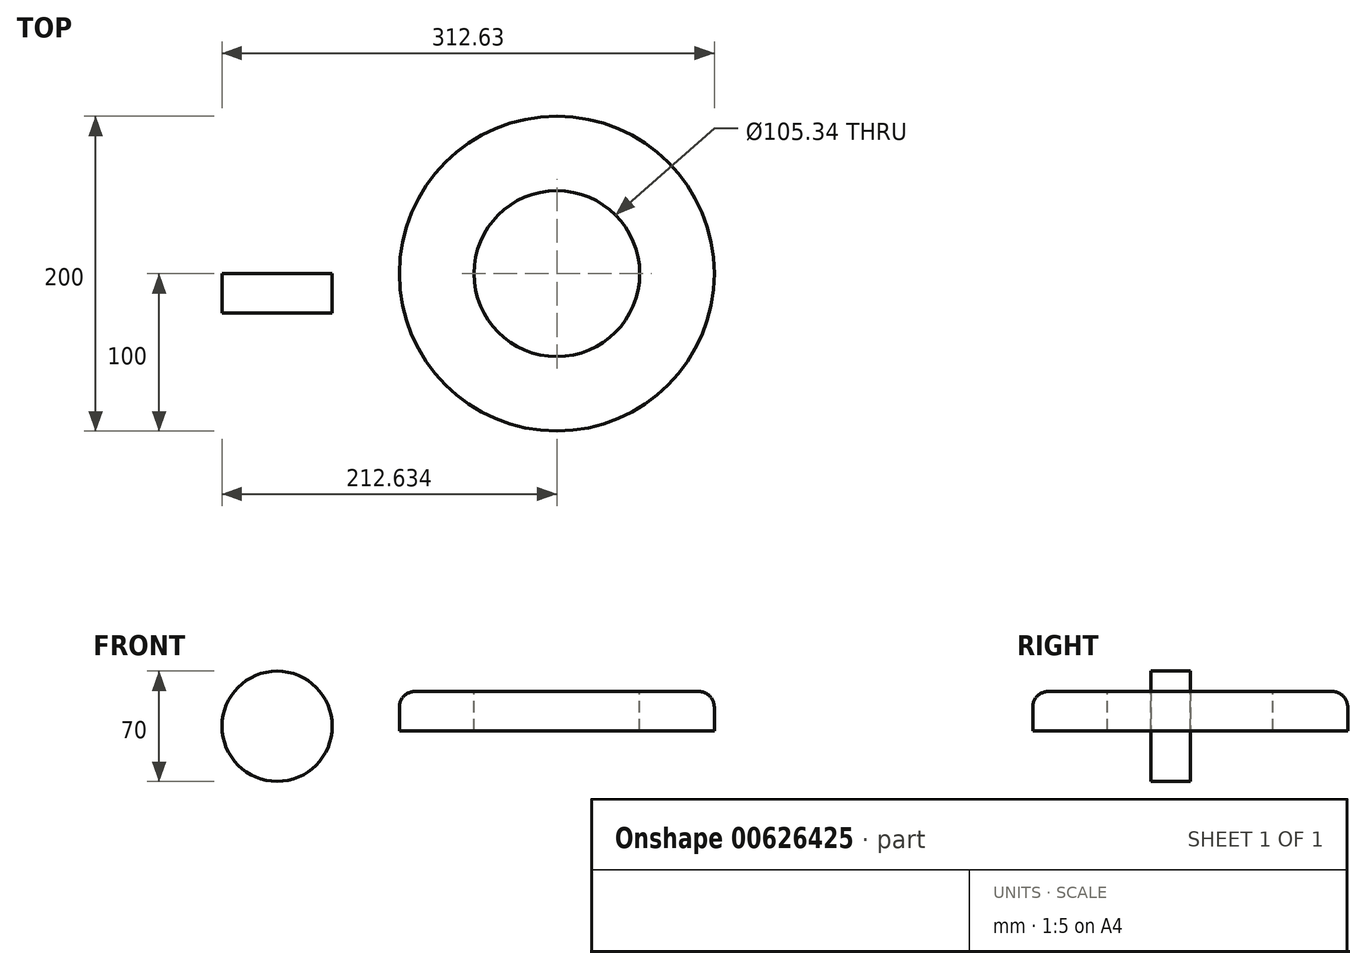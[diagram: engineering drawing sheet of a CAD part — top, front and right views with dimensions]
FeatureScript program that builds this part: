
annotation { "Feature Type Name" : "Feature", "Feature Type Description" : "" }
export const myFeature = defineFeature(function(context is Context, id is Id, definition is map)
    precondition{}
    {
        {
            var Q0;
            Q0=qCreatedBy(makeId("Front.planeOp"),FACE);
            var sketch = newSketch(context, id + "F0", { "sketchPlane" : qUnion([Q0])});
            skLineSegment(sketch, "E0.bottom", {"start": v(-39.69, 8.2) * mm, "end": v(60.31, 8.2) * mm});
            skLineSegment(sketch, "E0.top", {"start": v(-39.69, -16.8) * mm, "end": v(60.31, -16.8) * mm});
            skLineSegment(sketch, "E0.left", {"start": v(-39.69, 8.2) * mm, "end": v(-39.69, -16.8) * mm});
            skLineSegment(sketch, "E0.right", {"start": v(60.31, 8.2) * mm, "end": v(60.31, -16.8) * mm});
            skCircle(sketch, "E1", {"center": v(-117.32, -13.94) * mm, "radius": 35 * mm});
            skLineSegment(sketch, "E2", {"start": v(-39.69, 8.2) * mm, "end": v(-111.38, 20.55) * mm});
            skLineSegment(sketch, "E3", {"start": v(-39.69, -16.8) * mm, "end": v(-102.7, -45.75) * mm});
            skSolve(sketch);
        }
        {
            var Q0;
            {var subQ0=sQuery(id+"F0.wireOp",EDGE,"E1");var subQ1=makeQuery(id+"F0.imprint","INTERSECT",VERTEX,{"derivedFrom":[subQ0,sQuery(id+"F0.wireOp",EDGE,"E2")]});Q0=makeQuery(id+"F0.imprint","IMPRINT",FACE,{"disambiguationData":[TD([[makeQuery(id+"F0.imprint","IMPRINT",EDGE,{"disambiguationData":[TD([[subQ1,-1.0]])],"derivedFrom":subQ0}),1.0]])]});}
            extrude(context, id + "F1", {"entities" : qUnion([Q0]), "depth" : 25 * mm, "offsetDistance" : 25 * mm});
        }
        {
            var Q0;
            Q0=makeQuery(id+"F0.imprint","IMPRINT",FACE,{"disambiguationData":[TD([[makeQuery(id+"F0.imprint","IMPRINT",EDGE,{"derivedFrom":sQuery(id+"F0.wireOp",EDGE,"E0.bottom")}),-1.0]])]});
            var Q1;
            Q1=sQuery(id+"F0.wireOp",EDGE,"E0.right");
            revolve(context, id + "F2", {"entities" : qUnion([Q0]), "axis" : qUnion([Q1]), "revolveType" : RevolveType.FULL});
        }
        {
            var Q0;
            Q0=makeQuery(id+"F2.opRevolve","SWEPT_FACE",FACE,{"disambiguationData":[OSD([sQuery(id+"F0.wireOp",EDGE,"E0.bottom")])]});
            var sketch = newSketch(context, id + "F3", { "sketchPlane" : qUnion([Q0])});
            skCircle(sketch, "E4", {"center": v(60.31, 0) * mm, "radius": 52.67 * mm});
            skSolve(sketch);
        }
        {
            var Q0;
            Q0 = qSketchRegion(id + "F3", true);
            extrude(context, id + "F4", {"entities" : qUnion([Q0]), "operationType" : NewBodyOperationType.REMOVE, "endBound" : BoundingType.THROUGH_ALL, "oppositeDirection" : true, "depth" : 25 * mm, "offsetDistance" : 25 * mm});
        }
        {
            var Q0;
            Q0=makeQuery(id+"F2.opRevolve","SWEPT_EDGE",EDGE,{"disambiguationData":[OSD([sQuery(id+"F0.wireOp",EDGE,"E0.bottom"),sQuery(id+"F0.wireOp",EDGE,"E0.left"),sQuery(id+"F0.wireOp",EDGE,"E2")])]});
            fillet(context, id + "F5", {"entities" : qUnion([Q0]), "radius" : 10 * mm, "tangentPropagation" : true, "allowEdgeOverflow" : false});
        }
    });
